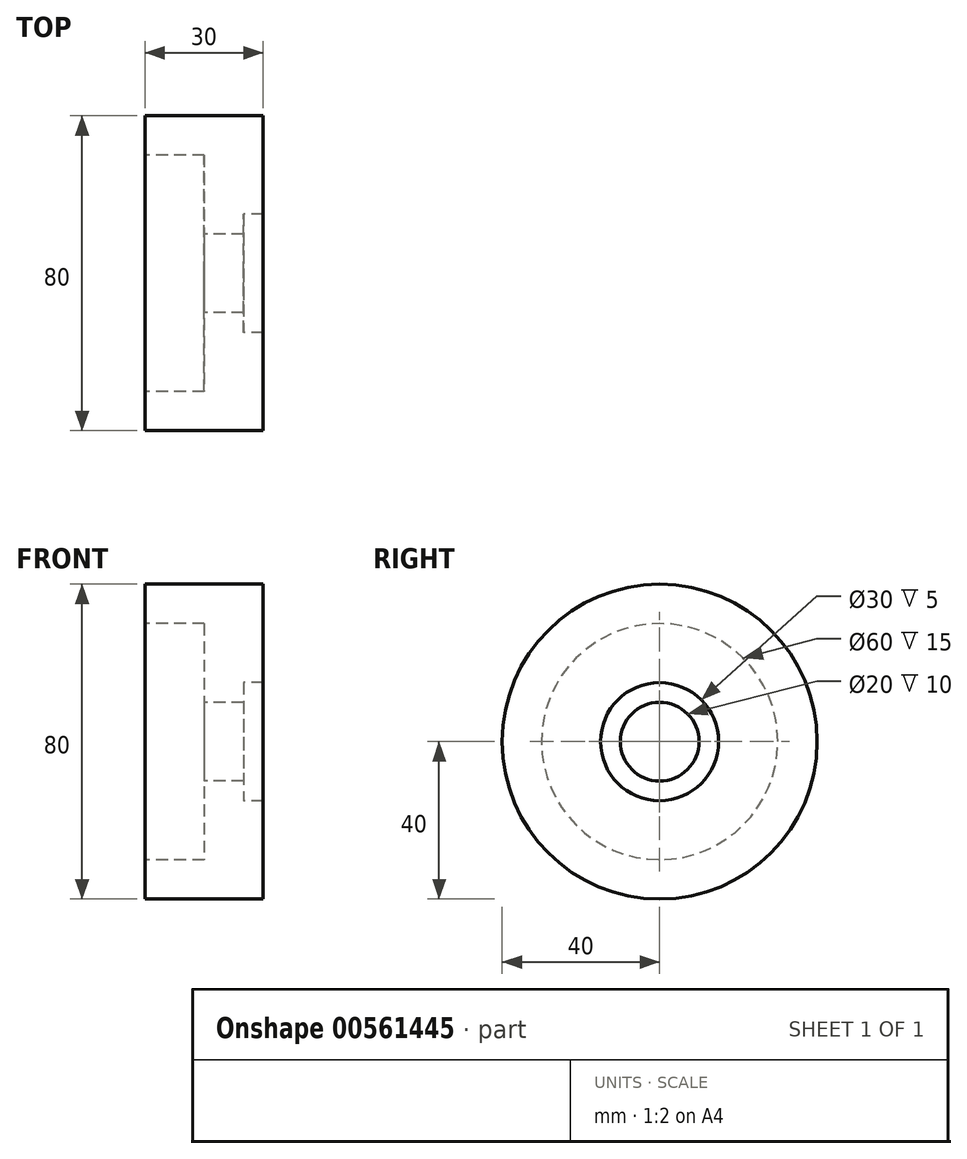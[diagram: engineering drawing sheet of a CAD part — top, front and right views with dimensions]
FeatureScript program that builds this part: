
annotation { "Feature Type Name" : "Feature", "Feature Type Description" : "" }
export const myFeature = defineFeature(function(context is Context, id is Id, definition is map)
    precondition{}
    {
        {
            var Q0;
            Q0=qCreatedBy(makeId("Front.planeOp"),FACE);
            var sketch = newSketch(context, id + "F0", { "sketchPlane" : qUnion([Q0])});
            skLineSegment(sketch, "E0", {"start": v(-30, 0) * mm, "end": v(0, 0) * mm, "construction": true});
            skLineSegment(sketch, "E1", {"start": v(0, 15) * mm, "end": v(0, 40) * mm});
            skLineSegment(sketch, "E2", {"start": v(0, 40) * mm, "end": v(-30, 40) * mm});
            skLineSegment(sketch, "E3", {"start": v(-30, 40) * mm, "end": v(-30, 30) * mm});
            skLineSegment(sketch, "E4", {"start": v(-30, 30) * mm, "end": v(-15, 30) * mm});
            skLineSegment(sketch, "E5", {"start": v(0, 15) * mm, "end": v(-5, 15) * mm});
            skPoint(sketch, "E6.trimOffspring.end.orphan", {"position": v(3.4, -40) * mm});
            skLineSegment(sketch, "E7", {"start": v(-5, 15) * mm, "end": v(-5, 10) * mm});
            skLineSegment(sketch, "E8", {"start": v(-15, 30) * mm, "end": v(-15, 10) * mm});
            skPoint(sketch, "E9", {"position": v(-15, 10) * mm});
            skLineSegment(sketch, "E10", {"start": v(-15, 10) * mm, "end": v(-5, 10) * mm});
            skLineSegment(sketch, "E11", {"start": v(0, 0) * mm, "end": v(0, 15) * mm, "construction": true});
            skPoint(sketch, "E12.MirrorP", {"position": v(-15, -10) * mm});
            skLineSegment(sketch, "E13.MirrorCS", {"start": v(0, -15) * mm, "end": v(0, -40) * mm});
            skLineSegment(sketch, "E14.MirrorCS", {"start": v(-15, -10) * mm, "end": v(-5, -10) * mm});
            skLineSegment(sketch, "E15.MirrorCS", {"start": v(-15, -30) * mm, "end": v(-15, -10) * mm});
            skLineSegment(sketch, "E16.MirrorCS", {"start": v(-5, -15) * mm, "end": v(-5, -10) * mm});
            skLineSegment(sketch, "E17.MirrorCS", {"start": v(-30, -40) * mm, "end": v(-30, -30) * mm});
            skLineSegment(sketch, "E18.MirrorCS", {"start": v(0, -15) * mm, "end": v(-5, -15) * mm});
            skLineSegment(sketch, "E19.MirrorCS", {"start": v(-30, -30) * mm, "end": v(-15, -30) * mm});
            skLineSegment(sketch, "E20.MirrorCS", {"start": v(0, -40) * mm, "end": v(-30, -40) * mm});
            skLineSegment(sketch, "E21.MirrorCS", {"start": v(0, 0) * mm, "end": v(0, -15) * mm, "construction": true});
            skLineSegment(sketch, "E22", {"start": v(-15, 10) * mm, "end": v(-15, -10) * mm});
            skLineSegment(sketch, "E23", {"start": v(-5, 10) * mm, "end": v(-5, -10) * mm});
            skLineSegment(sketch, "E24", {"start": v(0, 15) * mm, "end": v(0, -15) * mm});
            skSolve(sketch);
        }
        {
            var Q0;
            Q0=makeQuery(id+"F0.imprint","IMPRINT",FACE,{"disambiguationData":[TD([[makeQuery(id+"F0.imprint","IMPRINT",EDGE,{"derivedFrom":sQuery(id+"F0.wireOp",EDGE,"E1")}),1.0]])]});
            var Q1;
            Q1=sQuery(id+"F0.wireOp",EDGE,"E0");
            revolve(context, id + "F1", {"entities" : qUnion([Q0]), "axis" : qUnion([Q1]), "revolveType" : RevolveType.FULL});
        }
    });
